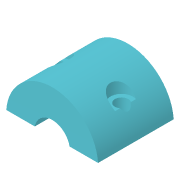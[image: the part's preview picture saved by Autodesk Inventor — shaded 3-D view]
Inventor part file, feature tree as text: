
AUTODESK INVENTOR PART (.ipt)
format: ipt  version: 2018 (Build 220112000, 112)  size: 135,168 bytes
history: native  units: in
note: dims shown in document units (in); Inventor stores cm internally (conversion verified against a paired STEP export)
features: extrude x3, sketch x3, plane x2, mirror x1
ambient origin geometry x8: Origin, YZ Plane, XZ Plane, XY Plane, X Axis, Y Axis, Z Axis, Center Point
bodies: Solid1 (feature_tree)
feature tree (9):
  extrude  "Extrusion1"  Depth=0.25in
  plane  "Work Plane2"
  extrude  "Extrusion2"  Depth=0.0234in
  extrude  "Extrusion3"  [1 undecoded]
  mirror  "Mirror1"
  sketch  "Sketch1"  dims[d0=0.65in d1=0.25in]
  plane  "Work Plane1"
  sketch  "Sketch2"  dims[d2=0.0469in d3=0.0234in]
  sketch  "Sketch3"  dims[d4=0.5344in d5=0.0in d6=-0.325in d7=0.0945in d8=0.2014in d9=0.1007in d10=0.5344in d11=0.2672in d12=1.0in d13=0.0in d14=0.1575in d15=0.1181in d16=0.0in]
note: 1 required parameter value undecoded (feature->parameter linkage not recoverable at this tier; creation-order binding heuristic only, values carry confidence <= 0.55)
